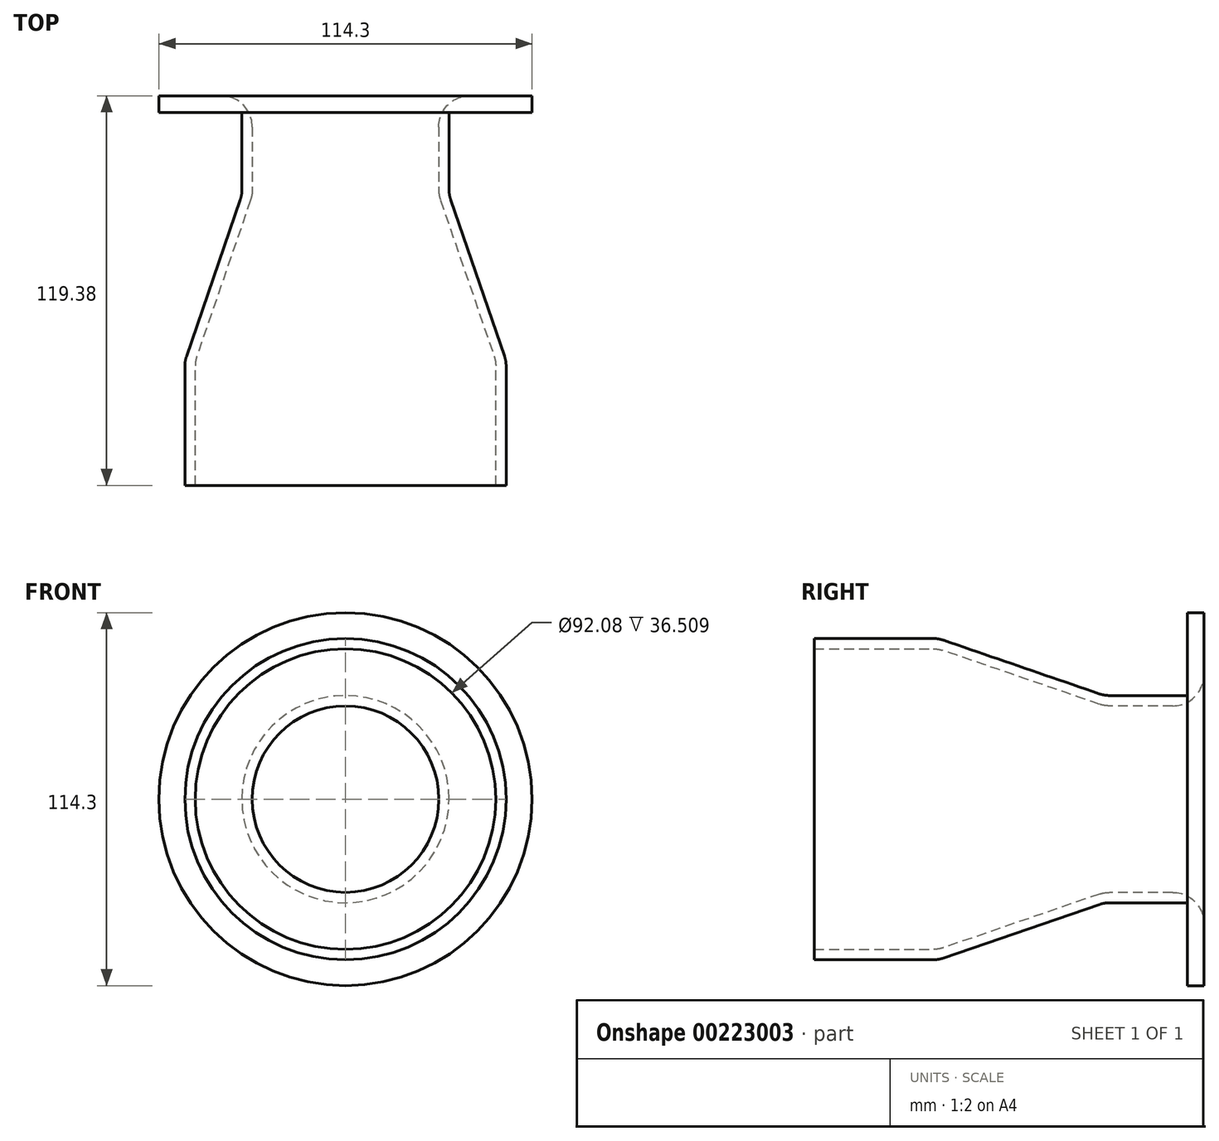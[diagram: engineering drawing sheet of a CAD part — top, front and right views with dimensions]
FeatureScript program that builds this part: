
annotation { "Feature Type Name" : "Feature", "Feature Type Description" : "" }
export const myFeature = defineFeature(function(context is Context, id is Id, definition is map)
    precondition{}
    {
        {
            var Q0;
            Q0=qCreatedBy(makeId("Front.planeOp"),FACE);
            var sketch = newSketch(context, id + "F0", { "sketchPlane" : qUnion([Q0])});
            skCircle(sketch, "E0", {"center": v(0, 0) * mm, "radius": 57.15 * mm});
            skSolve(sketch);
        }
        {
            var Q0;
            Q0 = qSketchRegion(id + "F0", true);
            extrude(context, id + "F1", {"entities" : qUnion([Q0]), "depth" : 5.08 * mm});
        }
        {
            var Q0;
            Q0=makeQuery(id+"F1.opExtrude","CAP_FACE",FACE,{"disambiguationData":[OSD([sQuery(id+"F0.wireOp",EDGE,"E0")])],"isStart":false});
            var sketch = newSketch(context, id + "F2", { "sketchPlane" : qUnion([Q0])});
            skCircle(sketch, "E1", {"center": v(0, 0) * mm, "radius": 31.75 * mm});
            skSolve(sketch);
        }
        {
            var Q0;
            Q0 = qSketchRegion(id + "F2", true);
            extrude(context, id + "F3", {"entities" : qUnion([Q0]), "operationType" : NewBodyOperationType.ADD, "depth" : 25.4 * mm});
        }
        {
            var Q0;
            Q0=makeQuery(id+"F3.opExtrude","CAP_FACE",FACE,{"disambiguationData":[OSD([sQuery(id+"F2.wireOp",EDGE,"E1")])],"isStart":false});
            var sketch = newSketch(context, id + "F4", { "sketchPlane" : qUnion([Q0])});
            skCircle(sketch, "E2", {"center": v(0, 0) * mm, "radius": 28.58 * mm});
            skSolve(sketch);
        }
        {
            var Q0;
            Q0 = qSketchRegion(id + "F4", true);
            extrude(context, id + "F5", {"entities" : qUnion([Q0]), "operationType" : NewBodyOperationType.REMOVE, "endBound" : BoundingType.THROUGH_ALL, "oppositeDirection" : true, "depth" : 25.4 * mm});
        }
        {
            var Q0;
            Q0=qCreatedBy(makeId("Right.planeOp"),FACE);
            var sketch = newSketch(context, id + "F6", { "sketchPlane" : qUnion([Q0])});
            skLineSegment(sketch, "E3", {"start": v(37.5, 0) * mm, "end": v(-75.2, 0) * mm, "construction": true});
            skLineSegment(sketch, "E4", {"start": v(-30.48, 28.57) * mm, "end": v(-30.48, 31.75) * mm});
            skLineSegment(sketch, "E5", {"start": v(-30.48, 31.75) * mm, "end": v(-81.28, 49.21) * mm});
            skLineSegment(sketch, "E6", {"start": v(-81.28, 49.21) * mm, "end": v(-81.28, 46.04) * mm});
            skLineSegment(sketch, "E7", {"start": v(-81.28, 0) * mm, "end": v(-30.48, 0) * mm});
            skLineSegment(sketch, "E8", {"start": v(-30.48, 28.57) * mm, "end": v(-81.28, 46.04) * mm});
            skSolve(sketch);
        }
        {
            var Q0;
            Q0 = qSketchRegion(id + "F6", true);
            var Q1;
            Q1=sQuery(id+"F6.wireOp",EDGE,"E3");
            revolve(context, id + "F7", {"operationType" : NewBodyOperationType.ADD, "entities" : qUnion([Q0]), "axis" : qUnion([Q1]), "revolveType" : RevolveType.FULL});
        }
        {
            var Q0;
            Q0=qCreatedBy(makeId("Right.planeOp"),FACE);
            var sketch = newSketch(context, id + "F8", { "sketchPlane" : qUnion([Q0])});
            skLineSegment(sketch, "E9", {"start": v(-81.28, 49.21) * mm, "end": v(-119.38, 49.21) * mm});
            skLineSegment(sketch, "E10", {"start": v(-119.38, 49.21) * mm, "end": v(-119.38, 46.04) * mm});
            skLineSegment(sketch, "E11", {"start": v(-119.38, 46.04) * mm, "end": v(-81.28, 46.04) * mm});
            skLineSegment(sketch, "E12", {"start": v(-81.28, 46.04) * mm, "end": v(-81.28, 49.21) * mm});
            skLineSegment(sketch, "E13", {"start": v(10.55, 0) * mm, "end": v(-137.38, 0) * mm, "construction": true});
            skSolve(sketch);
        }
        {
            var Q0;
            Q0 = qSketchRegion(id + "F8", true);
            var Q1;
            Q1=sQuery(id+"F8.wireOp",EDGE,"E13");
            revolve(context, id + "F9", {"operationType" : NewBodyOperationType.ADD, "entities" : qUnion([Q0]), "axis" : qUnion([Q1]), "revolveType" : RevolveType.FULL});
        }
        {
            var Q0;
            Q0=makeQuery(id+"F3.opExtrude","CAP_EDGE",EDGE,{"disambiguationData":[OSD([sQuery(id+"F2.wireOp",EDGE,"E1")])],"isStart":true});
            var Q1;
            Q1=makeQuery(id+"F7.boolean.opBoolean","MERGE",EDGE,{"derivedFrom":[makeQuery(id+"F3.opExtrude","CAP_EDGE",EDGE,{"disambiguationData":[OSD([sQuery(id+"F2.wireOp",EDGE,"E1")])],"isStart":false}),makeQuery(id+"F7.opRevolve","SWEPT_EDGE",EDGE,{"disambiguationData":[OSD([sQuery(id+"F6.wireOp",EDGE,"E4"),sQuery(id+"F6.wireOp",EDGE,"E5")])]})]});
            var Q2;
            Q2=makeQuery(id+"F9.boolean.opBoolean","MERGE",EDGE,{"derivedFrom":[makeQuery(id+"F7.opRevolve","SWEPT_EDGE",EDGE,{"disambiguationData":[OSD([sQuery(id+"F6.wireOp",EDGE,"E5"),sQuery(id+"F6.wireOp",EDGE,"E6")])]}),makeQuery(id+"F9.opRevolve","SWEPT_EDGE",EDGE,{"disambiguationData":[OSD([sQuery(id+"F8.wireOp",EDGE,"E9"),sQuery(id+"F8.wireOp",EDGE,"E12")])]})]});
            fillet(context, id + "F10", {"entities" : qUnion([Q0, Q1, Q2]), "radius" : 9.52 * mm, "tangentPropagation" : true, "allowEdgeOverflow" : false});
        }
        {
            var Q0;
            Q0=makeQuery(id+"F5.boolean.opBoolean","INTERSECT",EDGE,{"derivedFrom":[makeQuery(id+"F1.opExtrude","CAP_FACE",FACE,{"disambiguationData":[OSD([sQuery(id+"F0.wireOp",EDGE,"E0")])],"isStart":true}),makeQuery(id+"F5.opExtrude","SWEPT_FACE",FACE,{"disambiguationData":[OSD([sQuery(id+"F4.wireOp",EDGE,"E2")])]})]});
            var Q1;
            Q1=makeQuery(id+"F7.boolean.opBoolean","MERGE",EDGE,{"derivedFrom":[makeQuery(id+"F5.boolean.opBoolean","COPY",EDGE,{"derivedFrom":makeQuery(id+"F5.opExtrude","CAP_EDGE",EDGE,{"disambiguationData":[OSD([sQuery(id+"F4.wireOp",EDGE,"E2")])],"isStart":true})}),makeQuery(id+"F7.opRevolve","SWEPT_EDGE",EDGE,{"disambiguationData":[OSD([sQuery(id+"F6.wireOp",EDGE,"E4"),sQuery(id+"F6.wireOp",EDGE,"E8")])]})]});
            var Q2;
            Q2=makeQuery(id+"F9.boolean.opBoolean","MERGE",EDGE,{"derivedFrom":[makeQuery(id+"F7.opRevolve","SWEPT_EDGE",EDGE,{"disambiguationData":[OSD([sQuery(id+"F6.wireOp",EDGE,"E6"),sQuery(id+"F6.wireOp",EDGE,"E8")])]}),makeQuery(id+"F9.opRevolve","SWEPT_EDGE",EDGE,{"disambiguationData":[OSD([sQuery(id+"F8.wireOp",EDGE,"E11"),sQuery(id+"F8.wireOp",EDGE,"E12")])]})]});
            fillet(context, id + "F11", {"entities" : qUnion([Q0, Q1, Q2]), "radius" : 9.52 * mm, "tangentPropagation" : true, "allowEdgeOverflow" : false});
        }
    });
